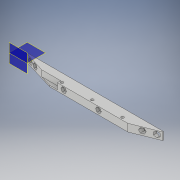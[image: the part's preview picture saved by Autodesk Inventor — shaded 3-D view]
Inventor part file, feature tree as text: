
AUTODESK INVENTOR PART (.ipt)
format: ipt  version: 2019 (Build 230136000, 136)  size: 178,176 bytes
history: native  units: in
note: dims shown in document units (in); Inventor stores cm internally (conversion verified against a paired STEP export)
features: plane x7, other x3
ambient origin geometry x8: Origin, YZ Plane, XZ Plane, XY Plane, X Axis, Y Axis, Z Axis, Center Point
bodies: Solid1 (feature_tree)
feature tree (10):
  other  "wheel_support_v5_narrow_with_line_sensor_all_holes_2mm_higher.ipt"
  other  "Solid1::wheel_support_v5_narrow_with_line_sensor_all_holes_2mm_higher.ipt"
  other  "TaggingFeature1"
  plane  "Work Plane1"
  plane  "Work Plane2"
  plane  "Work Plane3"
  plane  "Work Plane4"
  plane  "Work Plane5"
  plane  "Work Plane6"
  plane  "Work Plane7"
